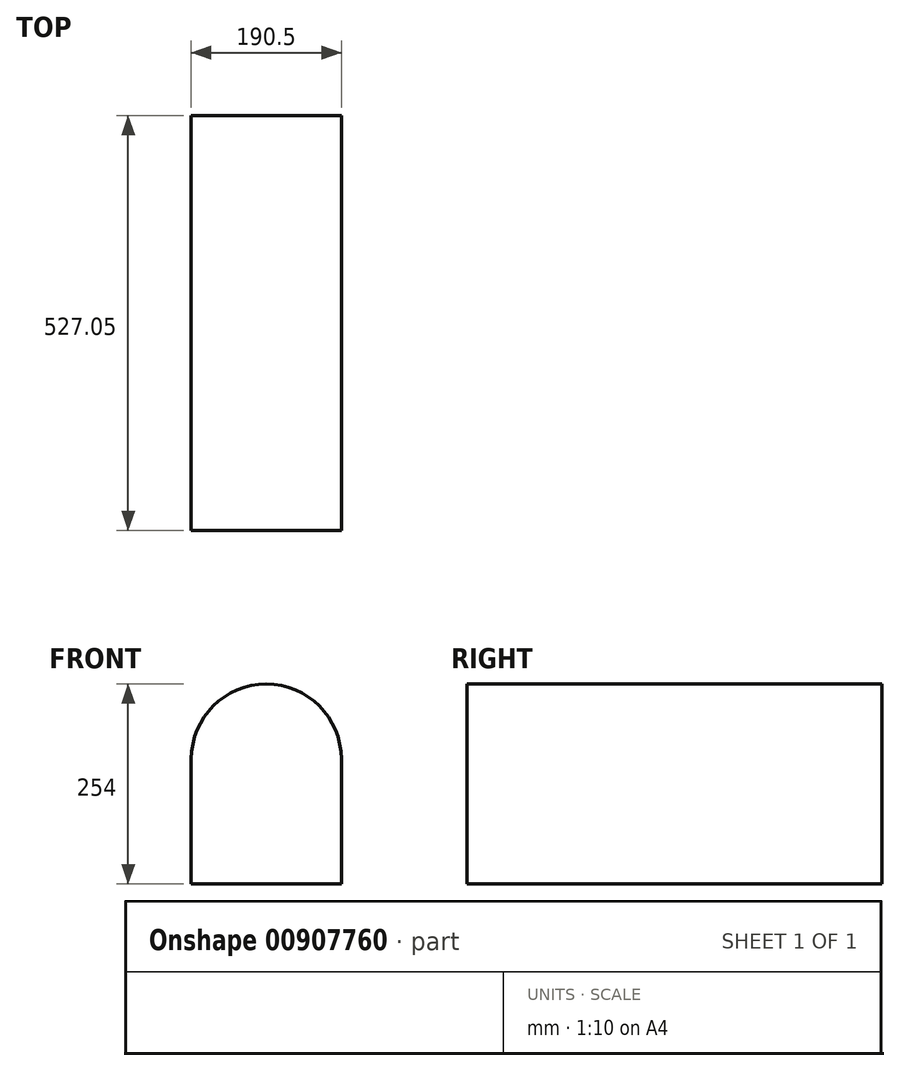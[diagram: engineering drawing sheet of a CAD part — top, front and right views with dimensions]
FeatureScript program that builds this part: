
annotation { "Feature Type Name" : "Feature", "Feature Type Description" : "" }
export const myFeature = defineFeature(function(context is Context, id is Id, definition is map)
    precondition{}
    {
        {
            var Q0;
            Q0=qCreatedBy(makeId("Front.planeOp"),FACE);
            var sketch = newSketch(context, id + "F0", { "sketchPlane" : qUnion([Q0])});
            skLineSegment(sketch, "E0", {"start": v(-95.25, 158.75) * mm, "end": v(-95.25, 0) * mm});
            skLineSegment(sketch, "E1", {"start": v(-95.25, 0) * mm, "end": v(95.25, 0) * mm});
            skLineSegment(sketch, "E2", {"start": v(95.25, 0) * mm, "end": v(95.25, 158.75) * mm});
            skArc(sketch, "E3", {"start": v(95.25, 158.75) * mm, "mid": v(0, 254) * mm, "end": v(-95.25, 158.75) * mm});
            skSolve(sketch);
        }
        {
            var Q0;
            Q0=makeQuery(id+"F0.imprint","IMPRINT",FACE,{"disambiguationData":[TD([[makeQuery(id+"F0.imprint","IMPRINT",EDGE,{"derivedFrom":sQuery(id+"F0.wireOp",EDGE,"E0")}),1.0]])]});
            extrude(context, id + "F1", {"entities" : qUnion([Q0]), "depth" : 527.05 * mm, "offsetDistance" : 25.4 * mm});
        }
    });
